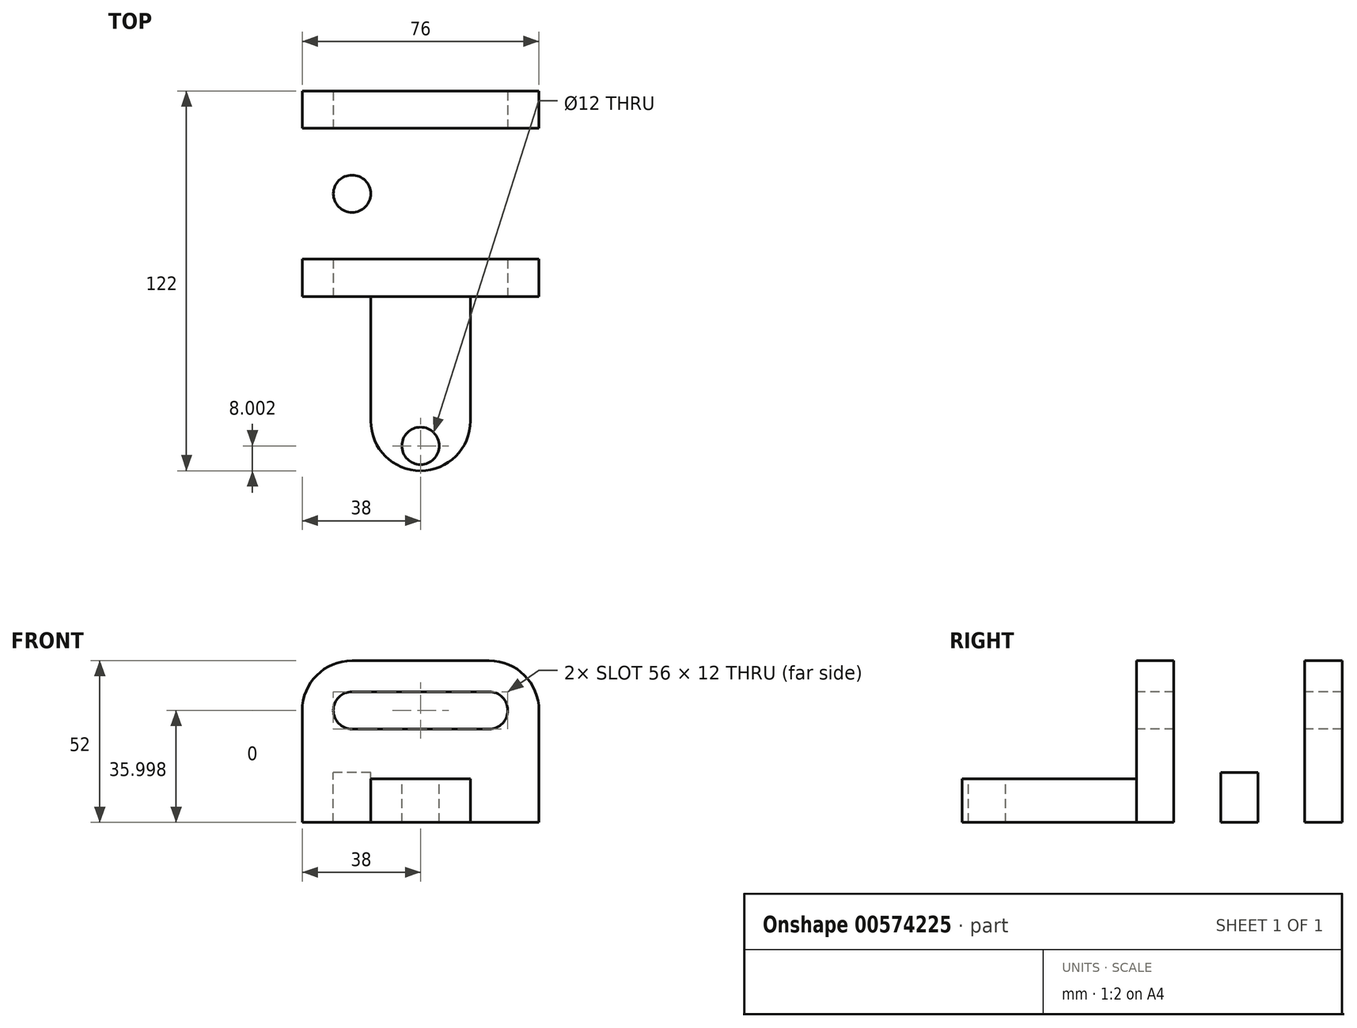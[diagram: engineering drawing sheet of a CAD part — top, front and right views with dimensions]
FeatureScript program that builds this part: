
annotation { "Feature Type Name" : "Feature", "Feature Type Description" : "" }
export const myFeature = defineFeature(function(context is Context, id is Id, definition is map)
    precondition{}
    {
        {
            var Q0;
            Q0=qCreatedBy(makeId("Right.planeOp"),FACE);
            var sketch = newSketch(context, id + "F0", { "sketchPlane" : qUnion([Q0])});
            skLineSegment(sketch, "E0", {"start": v(-33.88, -23.08) * mm, "end": v(32.12, -23.08) * mm});
            skLineSegment(sketch, "E1", {"start": v(-33.88, -23.08) * mm, "end": v(-33.88, 28.92) * mm});
            skLineSegment(sketch, "E2", {"start": v(-33.88, 28.92) * mm, "end": v(-21.88, 28.92) * mm});
            skLineSegment(sketch, "E3", {"start": v(-21.88, 28.92) * mm, "end": v(-21.88, -7.08) * mm});
            skLineSegment(sketch, "E4", {"start": v(-21.88, -7.08) * mm, "end": v(20.12, -7.08) * mm});
            skLineSegment(sketch, "E5", {"start": v(20.12, -7.08) * mm, "end": v(20.12, 28.92) * mm});
            skLineSegment(sketch, "E6", {"start": v(32.12, -23.08) * mm, "end": v(32.12, 28.92) * mm});
            skLineSegment(sketch, "E7", {"start": v(32.12, 28.92) * mm, "end": v(20.12, 28.92) * mm});
            skSolve(sketch);
        }
        {
            var Q0;
            Q0 = qSketchRegion(id + "F0", true);
            extrude(context, id + "F1", {"entities" : qUnion([Q0]), "depth" : 76 * mm, "offsetDistance" : 25 * mm});
        }
        {
            var Q0;
            Q0=makeQuery(id+"F1.opExtrude","CAP_EDGE",EDGE,{"disambiguationData":[OSD([sQuery(id+"F0.wireOp",EDGE,"E2")])],"isStart":false});
            var Q1;
            Q1=makeQuery(id+"F1.opExtrude","CAP_EDGE",EDGE,{"disambiguationData":[OSD([sQuery(id+"F0.wireOp",EDGE,"E7")])],"isStart":false});
            var Q2;
            Q2=makeQuery(id+"F1.opExtrude","CAP_EDGE",EDGE,{"disambiguationData":[OSD([sQuery(id+"F0.wireOp",EDGE,"E7")])],"isStart":true});
            var Q3;
            Q3=makeQuery(id+"F1.opExtrude","CAP_EDGE",EDGE,{"disambiguationData":[OSD([sQuery(id+"F0.wireOp",EDGE,"E2")])],"isStart":true});
            fillet(context, id + "F2", {"entities" : qUnion([Q0, Q1, Q2, Q3]), "radius" : 16 * mm, "tangentPropagation" : true, "allowEdgeOverflow" : false});
        }
        {
            var Q0;
            Q0=makeQuery(id+"F1.opExtrude","SWEPT_FACE",FACE,{"disambiguationData":[OSD([sQuery(id+"F0.wireOp",EDGE,"E1")])]});
            var sketch = newSketch(context, id + "F3", { "sketchPlane" : qUnion([Q0])});
            skLineSegment(sketch, "E8", {"start": v(16, 12.92) * mm, "end": v(60, 12.92) * mm, "construction": true});
            skLineSegment(sketch, "E9", {"start": v(16, 17.98) * mm, "end": v(16, 6.92) * mm, "construction": true});
            skArc(sketch, "E10", {"start": v(16, 18.92) * mm, "mid": v(10, 12.92) * mm, "end": v(16, 6.92) * mm});
            skArc(sketch, "E11", {"start": v(60, 6.92) * mm, "mid": v(66, 12.92) * mm, "end": v(60, 18.92) * mm});
            skLineSegment(sketch, "E12", {"start": v(16, 18.92) * mm, "end": v(60, 18.92) * mm});
            skLineSegment(sketch, "E13", {"start": v(16, 6.92) * mm, "end": v(60, 6.92) * mm});
            skSolve(sketch);
        }
        {
            var Q0;
            Q0=makeQuery(id+"F3.imprint","IMPRINT",FACE,{"disambiguationData":[TD([[makeQuery(id+"F3.imprint","IMPRINT",EDGE,{"derivedFrom":sQuery(id+"F3.wireOp",EDGE,"E10")}),1.0]])]});
            extrude(context, id + "F4", {"entities" : qUnion([Q0]), "operationType" : NewBodyOperationType.REMOVE, "endBound" : BoundingType.THROUGH_ALL, "oppositeDirection" : true, "depth" : 25 * mm, "offsetDistance" : 25 * mm});
        }
        {
            var Q0;
            Q0=makeQuery(id+"F1.opExtrude","SWEPT_FACE",FACE,{"disambiguationData":[OSD([sQuery(id+"F0.wireOp",EDGE,"E4")])]});
            var sketch = newSketch(context, id + "F5", { "sketchPlane" : qUnion([Q0])});
            skLineSegment(sketch, "E14", {"start": v(76, 20.12) * mm, "end": v(76, -0.88) * mm, "construction": true});
            skLineSegment(sketch, "E15", {"start": v(76, -0.88) * mm, "end": v(60, -0.88) * mm, "construction": true});
            skCircle(sketch, "E16", {"center": v(60, -0.88) * mm, "radius": 6 * mm});
            skLineSegment(sketch, "E17", {"start": v(38, -21.88) * mm, "end": v(38, 22.69) * mm, "construction": true});
            skPoint(sketch, "E17.endSnap0", {"position": v(38, 20.12) * mm});
            skCircle(sketch, "E18.MirrorC", {"center": v(16, -0.88) * mm, "radius": 6 * mm});
            skSolve(sketch);
        }
        {
            var Q0;
            Q0=makeQuery(id+"F5.imprint","IMPRINT",FACE,{"disambiguationData":[TD([[makeQuery(id+"F5.imprint","IMPRINT",EDGE,{"derivedFrom":sQuery(id+"F5.wireOp",EDGE,"E16")}),1.0]])]});
            var Q1;
            Q1=makeQuery(id+"F5.imprint","IMPRINT",FACE,{"disambiguationData":[TD([[makeQuery(id+"F5.imprint","IMPRINT",EDGE,{"derivedFrom":sQuery(id+"F5.wireOp",EDGE,"E18.MirrorC")}),-1.0]])]});
            extrude(context, id + "F6", {"entities" : qUnion([Q0, Q1]), "operationType" : NewBodyOperationType.REMOVE, "endBound" : BoundingType.THROUGH_ALL, "oppositeDirection" : true, "depth" : 25 * mm, "offsetDistance" : 25 * mm});
        }
        {
            var Q0;
            Q0=makeQuery(id+"F1.opExtrude","SWEPT_FACE",FACE,{"disambiguationData":[OSD([sQuery(id+"F0.wireOp",EDGE,"E1")])]});
            cPlane(context, id + "F7", {"entities" : qUnion([Q0]), "cplaneType" : CPlaneType.OFFSET, "offset" : 56 * mm, "width" : 150 * mm, "height" : 150 * mm});
        }
        {
            var Q0;
            Q0=qCreatedBy(id+"F7.planeOp",FACE);
            var sketch = newSketch(context, id + "F8", { "sketchPlane" : qUnion([Q0])});
            skLineSegment(sketch, "E19", {"start": v(76, -23.08) * mm, "end": v(54, -23.08) * mm, "construction": true});
            skLineSegment(sketch, "E20", {"start": v(54, -23.08) * mm, "end": v(22, -23.08) * mm});
            skLineSegment(sketch, "E21", {"start": v(54, -23.08) * mm, "end": v(54, -9.08) * mm});
            skLineSegment(sketch, "E22", {"start": v(54, -9.08) * mm, "end": v(22, -9.08) * mm});
            skLineSegment(sketch, "E23", {"start": v(22, -9.08) * mm, "end": v(22, -23.08) * mm});
            skSolve(sketch);
        }
        {
            var Q0;
            Q0 = qSketchRegion(id + "F8", true);
            extrude(context, id + "F9", {"entities" : qUnion([Q0]), "oppositeDirection" : true, "depth" : 56 * mm, "offsetDistance" : 25 * mm});
        }
        {
            var Q0;
            Q0=makeQuery(id+"F9.opExtrude","SWEPT_FACE",FACE,{"disambiguationData":[OSD([sQuery(id+"F8.wireOp",EDGE,"E22")])]});
            var sketch = newSketch(context, id + "F10", { "sketchPlane" : qUnion([Q0])});
            skLineSegment(sketch, "E24", {"start": v(38, -33.88) * mm, "end": v(38, -81.88) * mm, "construction": true});
            skPoint(sketch, "E24.endSnap0", {"position": v(38, -89.88) * mm});
            skCircle(sketch, "E25", {"center": v(38, -81.88) * mm, "radius": 6 * mm});
            skSolve(sketch);
        }
        {
            var Q0;
            Q0=makeQuery(id+"F9.opExtrude","CAP_EDGE",EDGE,{"disambiguationData":[OSD([sQuery(id+"F8.wireOp",EDGE,"E21")])],"isStart":true});
            var Q1;
            Q1=makeQuery(id+"F9.opExtrude","CAP_EDGE",EDGE,{"disambiguationData":[OSD([sQuery(id+"F8.wireOp",EDGE,"E23")])],"isStart":true});
            fillet(context, id + "F11", {"entities" : qUnion([Q0, Q1]), "radius" : 16 * mm, "tangentPropagation" : true, "allowEdgeOverflow" : false});
        }
        {
            var Q0;
            Q0=makeQuery(id+"F10.imprint","IMPRINT",FACE,{"disambiguationData":[TD([[makeQuery(id+"F10.imprint","IMPRINT",EDGE,{"derivedFrom":sQuery(id+"F10.wireOp",EDGE,"E25")}),1.0]])]});
            extrude(context, id + "F12", {"entities" : qUnion([Q0]), "operationType" : NewBodyOperationType.REMOVE, "endBound" : BoundingType.THROUGH_ALL, "oppositeDirection" : true, "depth" : 25 * mm, "offsetDistance" : 25 * mm});
        }
    });
